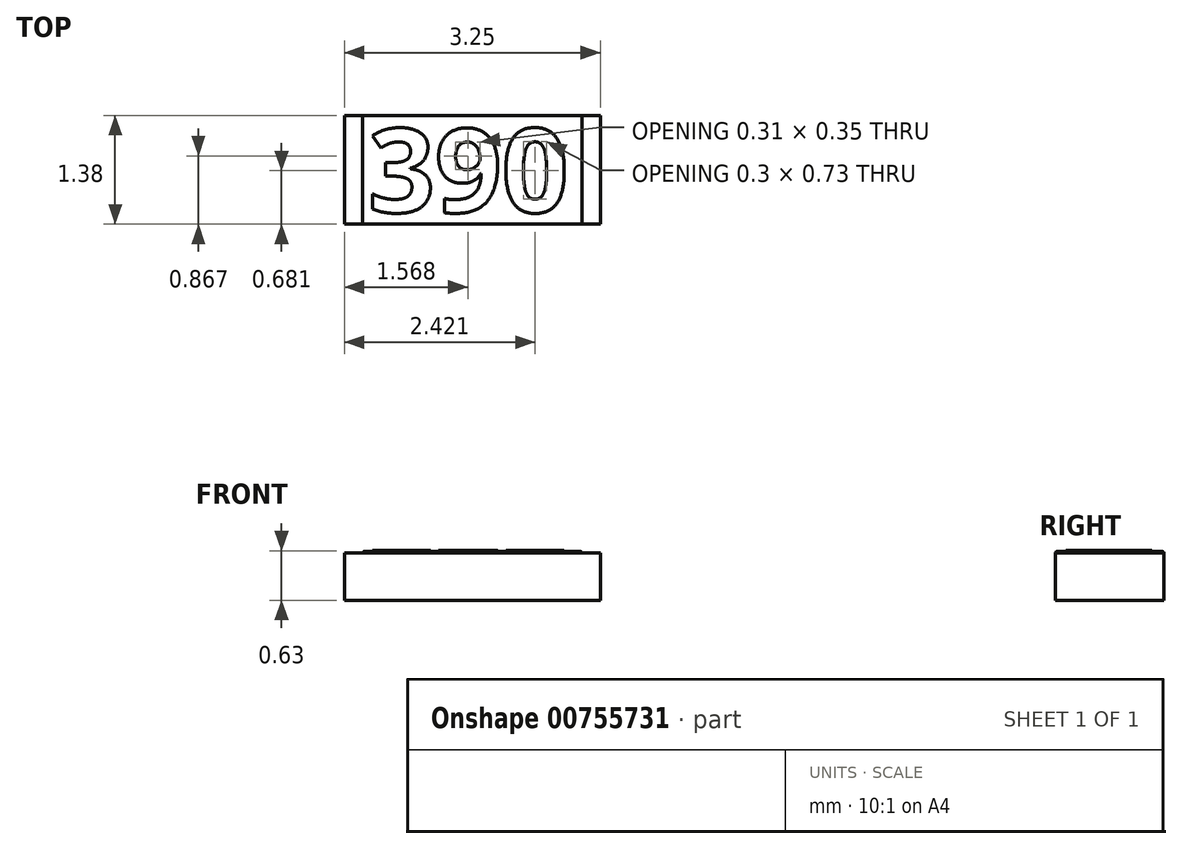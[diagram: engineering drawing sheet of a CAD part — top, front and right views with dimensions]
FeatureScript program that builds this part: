
annotation { "Feature Type Name" : "Feature", "Feature Type Description" : "" }
export const myFeature = defineFeature(function(context is Context, id is Id, definition is map)
    precondition{}
    {
        {
            var Q0;
            Q0=qCreatedBy(makeId("Top.planeOp"),FACE);
            var sketch = newSketch(context, id + "F0", { "sketchPlane" : qUnion([Q0])});
            skLineSegment(sketch, "E0.bottom", {"start": v(0, 0) * mm, "end": v(3.25, 0) * mm});
            skLineSegment(sketch, "E0.top", {"start": v(0, 1.38) * mm, "end": v(3.25, 1.38) * mm});
            skLineSegment(sketch, "E0.left", {"start": v(0, 0) * mm, "end": v(0, 1.38) * mm});
            skLineSegment(sketch, "E0.right", {"start": v(3.25, 0) * mm, "end": v(3.25, 1.38) * mm});
            skLineSegment(sketch, "E1", {"start": v(0, 0.7) * mm, "end": v(3.25, 0.7) * mm, "construction": true});
            skLineSegment(sketch, "E2", {"start": v(1.63, 0) * mm, "end": v(1.63, 1.38) * mm, "construction": true});
            skSolve(sketch);
        }
        {
            var Q0;
            Q0 = qSketchRegion(id + "F0", true);
            var Q1;
            Q1=makeQuery(id+"F0.imprint","IMPRINT",FACE,{"disambiguationData":[TD([[makeQuery(id+"F0.imprint","IMPRINT",EDGE,{"derivedFrom":sQuery(id+"F0.wireOp",EDGE,"E0.bottom")}),1.0]])]});
            extrude(context, id + "F1", {"entities" : qUnion([Q0, Q1]), "depth" : 0.6 * mm, "offsetDistance" : 25 * mm});
        }
        {
            var Q0;
            Q0=makeQuery(id+"F1.opExtrude","CAP_FACE",FACE,{"disambiguationData":[OSD([sQuery(id+"F0.wireOp",EDGE,"E0.bottom"),sQuery(id+"F0.wireOp",EDGE,"E0.top"),sQuery(id+"F0.wireOp",EDGE,"E0.left"),sQuery(id+"F0.wireOp",EDGE,"E0.right")])],"isStart":false});
            var sketch = newSketch(context, id + "F2", { "sketchPlane" : qUnion([Q0])});
            skLineSegment(sketch, "E3.bottom", {"start": v(0.23, 1.38) * mm, "end": v(3.02, 1.38) * mm});
            skLineSegment(sketch, "E3.top", {"start": v(0.23, 0) * mm, "end": v(3.02, 0) * mm});
            skLineSegment(sketch, "E3.left", {"start": v(0.23, 1.38) * mm, "end": v(0.23, 0) * mm});
            skLineSegment(sketch, "E3.right", {"start": v(3.02, 1.38) * mm, "end": v(3.02, 0) * mm});
            skSolve(sketch);
        }
        {
            var Q0;
            Q0=makeQuery(id+"F2.imprint","IMPRINT",FACE,{"disambiguationData":[TD([[makeQuery(id+"F2.imprint","IMPRINT",EDGE,{"derivedFrom":sQuery(id+"F2.wireOp",EDGE,"E3.bottom")}),-1.0]])]});
            extrude(context, id + "F3", {"entities" : qUnion([Q0]), "depth" : 0.02 * mm, "offsetDistance" : 25 * mm});
        }
        {
            var Q0;
            Q0=makeQuery(id+"F3.opExtrude","CAP_FACE",FACE,{"disambiguationData":[OSD([sQuery(id+"F2.wireOp",EDGE,"E3.bottom"),sQuery(id+"F2.wireOp",EDGE,"E3.top"),sQuery(id+"F2.wireOp",EDGE,"E3.left"),sQuery(id+"F2.wireOp",EDGE,"E3.right")])],"isStart":false});
            fillet(context, id + "F4", {"entities" : qUnion([Q0]), "radius" : 0.02 * mm, "tangentPropagation" : true, "allowEdgeOverflow" : false});
        }
        {
            var Q0;
            Q0=makeQuery(id+"F3.opExtrude","CAP_FACE",FACE,{"disambiguationData":[OSD([sQuery(id+"F2.wireOp",EDGE,"E3.bottom"),sQuery(id+"F2.wireOp",EDGE,"E3.top"),sQuery(id+"F2.wireOp",EDGE,"E3.left"),sQuery(id+"F2.wireOp",EDGE,"E3.right")])],"isStart":false});
            var sketch = newSketch(context, id + "F5", { "sketchPlane" : qUnion([Q0])});
            skText(sketch, "E4", { "text": "390", "fontName": "OpenSans-Bold.ttf"});
            const initialGuessF5  = {"E4": [0.0003, 0.00015, 1, 0, 0.00107]};
            skSetInitialGuess(sketch, initialGuessF5);
            skSolve(sketch);
        }
        {
            var Q0;
            Q0 = qSketchRegion(id + "F5", true);
            extrude(context, id + "F6", {"entities" : qUnion([Q0]), "depth" : 0.01 * mm, "offsetDistance" : 25 * mm});
        }
    });
